# Revit family: Rohrschelle Titan HD, M16, Gummi
name_source: partatom
category: HLS-Bauteile
revit_build: Autodesk Revit 2017 (Build: 20190507_1515(x64)
units: mm (PartAtom-declared; Revit-internal decimal feet)

## family parameters
Arbeitsebenenbasiert = Ja
Beim Laden mit Abzugskörper schneiden = Nein
Bemaßung runder Anschluss = Durchmesser verwenden
Gemeinsam genutzt = Ja
Immer vertikal = Nein
Raumberechnungspunkt = Nein
Teiletyp = Normal

## types (33) — shared parameters
A = 26 mm  [stored 0.0853018 ft]
Anschluss = M16
Anschlußhöhe = 26 mm
Bauart = zweiteilig
Baustoffklasse = B2
Brandschutz = RAL GZ 656
DF1 = 29 mm  [stored 0.0951444 ft]
DS = 6 mm  [stored 0.019685 ft]
DVS = 13 mm
Dämmstärke = 6 mm  [stored 0.019685 ft]
Fabrikat = MEFA
Farbe Schalldämmeinlage = schwarz
Firma = MEFA Befestigungs- und Montagesysteme GmbH
HGA = 15 mm  [stored 0.0492126 ft]
Kurztext1 = Rohrschelle Titan HD 50x5,0
MB = 50 mm  [stored 0.164042 ft]
MD = 5 mm  [stored 0.0164042 ft]
Material = Stahl
Material Schalldämmeinlage = TPE
Materialmaße = 50x5,0 mm
Materialname = S235
Mengeneinheit = St
Oberflaeche = galvanisch verzinkt
Schalldämmeinlage = Gummi
Verschluss = Schraubverschluss
Verschluss-Schraube = M12
Vorgabe-Ansicht = 1219 mm
max. Temperaturbeständigkeit = 100 °C
max. zul. Last horizontal = 0.00 kN
max. zul. Last vertikal = 0.00 kN
vpe = 1 St
zero-valued in all types: Nennweite DN Rohr, Stärke Material, max. Rohraußendurchmesser, min. Rohraußendurchmesser

## per-type parameters (varying)
| type | Achsabstand | Artikelnummer | B | Breite | D | D0 | DF2 | EAN | Gewicht | Gewicht pro Bauteil | H | Höhe | Kurztext2 | R | RM | Rohraußendurchmesser | Rohraußendurchmesser Zoll | S | max. Höhe | max. zul. Last |
| Titan HD, M16, Ø 64, Gummi | 125 mm | 0071516 | 154 mm | 154 mm | 64 mm  [stored 0.209974 ft] | 76 mm  [stored 0.249344 ft] | 19 mm  [stored 0.062336 ft] | 4250928403261 | 0.94 kg | 0.94 kg | 101 mm | 101 mm | 64 mm M16 TPE | 38 mm  [stored 0.124672 ft] | 43 mm | 64 mm  [stored 0.209974 ft] | Zoll | 125 mm | 101 mm | 3.20 kN |
| Titan HD, M16, Ø 76, Gummi | 137 mm | 0071520 | 166 mm | 166 mm | 76 mm  [stored 0.249344 ft] | 88 mm  [stored 0.288714 ft] | 19 mm  [stored 0.062336 ft] | 4250928403285 | 1.03 kg | 1.03 kg | 113 mm | 113 mm | 76 mm M16 TPE | 44 mm  [stored 0.144357 ft] | 49 mm | 76 mm  [stored 0.249344 ft] | 2 1/2 Zoll | 137 mm | 113 mm | 3.20 kN |
| Titan HD, M16, Ø 89, Gummi | 150 mm | 0071522 | 179 mm | 179 mm | 89 mm  [stored 0.291995 ft] | 101 mm | 19 mm  [stored 0.062336 ft] | 4250928403308 | 1.12 kg | 1.12 kg | 126 mm | 126 mm | 89 mm M16 TPE | 51 mm | 56 mm | 89 mm  [stored 0.291995 ft] | 3 Zoll | 150 mm | 126 mm | 3.20 kN |
| Titan HD, M16, Ø108, Gummi | 169 mm | 0071528 | 199 mm | 198 mm | 108 mm | 120 mm | 20 mm  [stored 0.0656168 ft] | 4250928403322 | 1.27 kg | 1.27 kg | 145 mm | 145 mm | 108 mm M16 TPE | 60 mm  [stored 0.19685 ft] | 65 mm | 108 mm | Zoll | 170 mm | 145 mm | 3.20 kN |
| Titan HD, M16, Ø110, Gummi | 171 mm | 0071536 | 201 mm | 200 mm | 110 mm | 122 mm | 20 mm  [stored 0.0656168 ft] | 4250928403353 | 1.28 kg | 1.28 kg | 147 mm | 147 mm | 110 mm M16 TPE | 61 mm  [stored 0.200131 ft] | 66 mm | 110 mm | Zoll | 172 mm | 147 mm | 3.20 kN |
| Titan HD, M16, Ø133, Gummi | 195 mm | 0071609 | 224 mm | 224 mm | 133 mm | 145 mm | 20 mm  [stored 0.0656168 ft] | 4250928403414 | 1.45 kg | 1.45 kg | 170 mm | 170 mm | 133 mm M16 TPE | 73 mm | 78 mm | 133 mm | Zoll | 195 mm | 170 mm | 3.20 kN |
| Titan HD, M16, Ø135, Gummi | 197 mm | 0071617 | 226 mm | 226 mm | 135 mm | 147 mm | 20 mm  [stored 0.0656168 ft] | 4250928403438 | 1.47 kg | 1.47 kg | 172 mm | 172 mm | 135 mm M16 TPE | 74 mm | 79 mm | 135 mm | Zoll | 197 mm | 172 mm | 3.20 kN |
| Titan HD, M16, Ø140, Gummi | 202 mm | 0071625 | 231 mm | 231 mm | 140 mm | 152 mm | 20 mm  [stored 0.0656168 ft] | 4250928403445 | 1.51 kg | 1.51 kg | 177 mm | 177 mm | 140 mm M16 TPE | 76 mm  [stored 0.249344 ft] | 81 mm  [stored 0.265748 ft] | 140 mm | 5 Zoll | 202 mm | 177 mm | 3.20 kN |
| Titan HD, M16, Ø160, Gummi | 221 mm | 0071684 | 251 mm | 250 mm | 160 mm | 172 mm | 20 mm  [stored 0.0656168 ft] | 4250928403476 | 1.66 kg | 1.66 kg | 197 mm | 197 mm | 160 mm M16 TPE | 86 mm  [stored 0.282152 ft] | 91 mm  [stored 0.298556 ft] | 160 mm | Zoll | 222 mm | 197 mm | 3.20 kN |
| Titan HD, M16, Ø165, Gummi | 227 mm | 0071692 | 256 mm | 256 mm | 165 mm | 177 mm | 20 mm  [stored 0.0656168 ft] | 4250928403506 | 1.69 kg | 1.69 kg | 202 mm | 202 mm | 165 mm M16 TPE | 89 mm  [stored 0.291995 ft] | 94 mm | 165 mm | 6 Zoll | 227 mm | 202 mm | 3.20 kN |
| Titan HD, M16, Ø168, Gummi | 230 mm | 0071714 | 259 mm | 259 mm | 168 mm | 180 mm | 20 mm  [stored 0.0656168 ft] | 4250928403513 | 1.72 kg | 1.72 kg | 205 mm | 205 mm | 168 mm M16 TPE | 90 mm | 95 mm | 168 mm | Zoll | 230 mm | 205 mm | 3.20 kN |
| Titan HD, M16, Ø194, Gummi | 257 mm | 0071773 | 286 mm | 286 mm | 194 mm | 206 mm | 20 mm  [stored 0.0656168 ft] | 4250928403551 | 1.91 kg | 1.91 kg | 231 mm | 231 mm | 194 mm M16 TPE | 103 mm | 108 mm | 194 mm | Zoll | 257 mm | 231 mm | 11.50 kN |
| Titan HD, M16, Ø200, Gummi | 261 mm | 0071781 | 292 mm | 290 mm | 200 mm | 212 mm | 20 mm  [stored 0.0656168 ft] | 4250928403575 | 1.96 kg | 1.96 kg | 237 mm | 237 mm | 200 mm M16 TPE | 106 mm | 111 mm | 200 mm | Zoll | 263 mm | 237 mm | 11.50 kN |
| Titan HD, M16, Ø210, Gummi | 261 mm | 0071803 | 302 mm | 290 mm | 210 mm | 222 mm | 20 mm  [stored 0.0656168 ft] | 4250928403575 | 1.96 kg | 1.96 kg | 247 mm | 237 mm | 200 mm M16 TPE | 111 mm | 116 mm | 200 mm | Zoll | 273 mm | 237 mm | 11.50 kN |
| Titan HD, M16, Ø219, Gummi | 282 mm | 0071838 | 311 mm | 311 mm | 219 mm | 231 mm | 20 mm  [stored 0.0656168 ft] | 4250928403612 | 2.10 kg | 2.10 kg | 256 mm | 256 mm | 219 mm M16 TPE | 116 mm | 121 mm | 219 mm | 8 Zoll | 282 mm | 256 mm | 11.50 kN |
| Titan HD, M16, Ø267, Gummi | 330 mm | 0071897 | 359 mm | 359 mm | 267 mm | 279 mm | 20 mm  [stored 0.0656168 ft] | 4250928403650 | 2.46 kg | 2.46 kg | 304 mm | 304 mm | 267 mm M16 TPE | 140 mm | 145 mm | 267 mm | Zoll | 330 mm | 304 mm | 11.50 kN |
| Titan HD, M16, Ø273, Gummi | 336 mm | 0071900 | 365 mm | 365 mm | 273 mm | 285 mm | 20 mm  [stored 0.0656168 ft] | 4250928403674 | 2.50 kg | 2.50 kg | 310 mm | 310 mm | 273 mm M16 TPE | 143 mm | 148 mm | 273 mm | 10 Zoll | 336 mm | 310 mm | 11.50 kN |
| Titan HD, M16, Ø324, Gummi | 387 mm | 0071943 | 416 mm | 416 mm | 324 mm | 336 mm | 20 mm  [stored 0.0656168 ft] | 4250928403711 | 2.88 kg | 2.88 kg | 361 mm | 361 mm | 324 mm M16 TPE | 168 mm | 173 mm | 324 mm | 12 Zoll | 387 mm | 361 mm | 11.50 kN |
| Titan HD, M16, Ø356, Gummi | 419 mm | 0071978 | 448 mm | 448 mm | 356 mm | 368 mm | 20 mm  [stored 0.0656168 ft] | 4250928403735 | 3.12 kg | 3.12 kg | 393 mm | 393 mm | 356 mm M16 TPE | 184 mm | 189 mm | 356 mm | Zoll | 419 mm | 393 mm | 11.50 kN |
| Titan HD, M16, Ø368, Gummi | 431 mm | 0071986 | 460 mm | 460 mm | 368 mm | 380 mm | 20 mm  [stored 0.0656168 ft] | 4250928403759 | 3.21 kg | 3.21 kg | 405 mm | 405 mm | 368 mm M16 TPE | 190 mm | 195 mm | 368 mm | Zoll | 431 mm | 405 mm | 11.50 kN |
| Titan HD, M16, Ø114, Gummi | 175 mm | 0071552 | 205 mm | 204 mm | 114 mm | 126 mm | 20 mm  [stored 0.0656168 ft] | 4250928403360 | 1.31 kg | 1.31 kg | 151 mm | 151 mm | 114 mm M16 TPE | 63 mm  [stored 0.206693 ft] | 68 mm  [stored 0.223097 ft] | 114 mm | 4 Zoll | 176 mm | 151 mm | 3.20 kN |
| Titan HD, M16, Ø125, Gummi | 175 mm | 0071552 | 216 mm | 204 mm | 125 mm | 137 mm | 20 mm  [stored 0.0656168 ft] | 4250928403360 | 1.31 kg | 1.31 kg | 162 mm | 151 mm | 114 mm M16 TPE | 69 mm | 74 mm | 114 mm | 4 Zoll | 187 mm | 151 mm | 3.20 kN |
| Titan HD, M16, Ø127, Gummi | 188 mm | 0071595 | 218 mm | 217 mm | 127 mm | 139 mm | 20 mm  [stored 0.0656168 ft] | 4250928403391 | 1.41 kg | 1.41 kg | 164 mm | 164 mm | 127 mm M16 TPE | 70 mm | 75 mm | 127 mm | Zoll | 189 mm | 164 mm | 3.20 kN |
| Titan HD, M16, Ø152, Gummi | 214 mm | 0071641 | 243 mm | 243 mm | 152 mm | 164 mm | 20 mm  [stored 0.0656168 ft] | 4250928403452 | 1.60 kg | 1.60 kg | 189 mm | 189 mm | 152 mm M16 TPE | 82 mm  [stored 0.269029 ft] | 87 mm  [stored 0.285433 ft] | 152 mm | Zoll | 214 mm | 189 mm | 3.20 kN |
| Titan HD, M16, Ø177, Gummi | 239 mm | 0071730 | 268 mm | 268 mm | 177 mm | 189 mm | 20 mm  [stored 0.0656168 ft] | 4250928403520 | 1.78 kg | 1.78 kg | 214 mm | 214 mm | 177 mm M16 TPE | 95 mm | 100 mm | 177 mm | Zoll | 239 mm | 214 mm | 11.50 kN |
| Titan HD, M16, Ø180, Gummi | 242 mm | 0071757 | 271 mm | 271 mm | 180 mm | 192 mm | 20 mm  [stored 0.0656168 ft] | 4250928403537 | 1.81 kg | 1.81 kg | 217 mm | 217 mm | 180 mm M16 TPE | 96 mm | 101 mm | 180 mm | Zoll | 242 mm | 217 mm | 11.50 kN |
| Titan HD, M16, Ø225, Gummi | 286 mm | 0071846 | 317 mm | 315 mm | 225 mm | 237 mm | 20 mm  [stored 0.0656168 ft] | 4250928403629 | 2.14 kg | 2.14 kg | 262 mm | 262 mm | 225 mm M16 TPE | 119 mm | 124 mm | 225 mm | Zoll | 288 mm | 262 mm | 11.50 kN |
| Titan HD, M16, Ø245, Gummi | 308 mm | 0071870 | 337 mm | 337 mm | 245 mm | 257 mm | 20 mm  [stored 0.0656168 ft] | 4250928403636 | 2.29 kg | 2.29 kg | 282 mm | 282 mm | 245 mm M16 TPE | 129 mm | 134 mm | 245 mm | Zoll | 308 mm | 282 mm | 11.50 kN |
| Titan HD, M16, Ø280, Gummi | 343 mm | 0071927 | 372 mm | 372 mm | 280 mm | 292 mm | 20 mm  [stored 0.0656168 ft] | 4250928403681 | 2.56 kg | 2.56 kg | 317 mm | 317 mm | 280 mm M16 TPE | 146 mm | 151 mm | 280 mm | Zoll | 343 mm | 317 mm | 11.50 kN |
| Titan HD, M16, Ø298, Gummi | 361 mm | 0071935 | 390 mm | 390 mm | 298 mm | 310 mm | 20 mm  [stored 0.0656168 ft] | 4250928403698 | 2.69 kg | 2.69 kg | 335 mm | 335 mm | 298 mm M16 TPE | 155 mm | 160 mm | 298 mm | Zoll | 361 mm | 335 mm | 11.50 kN |
| Titan HD, M16, Ø406, Gummi | 469 mm | 0071994 | 498 mm | 498 mm | 406 mm | 418 mm | 20 mm  [stored 0.0656168 ft] | 4250928403773 | 3.50 kg | 3.50 kg | 443 mm | 443 mm | 406 mm M16 TPE | 209 mm | 214 mm | 406 mm | Zoll | 469 mm | 443 mm | 11.50 kN |
| Titan HD, M16, Ø457, Gummi | 520 mm | 0072003 | 549 mm | 549 mm | 457 mm | 469 mm | 20 mm  [stored 0.0656168 ft] | 4250928403780 | 3.88 kg | 3.88 kg | 494 mm | 494 mm | 457 mm M16 TPE | 235 mm | 240 mm | 457 mm | Zoll | 520 mm | 494 mm | 11.50 kN |
| Titan HD, M16, Ø508, Gummi | 571 mm | 0072014 | 600 mm | 600 mm | 508 mm | 520 mm | 20 mm  [stored 0.0656168 ft] | 4250928403803 | 4.26 kg | 4.26 kg | 545 mm | 545 mm | 508 mm M16 TPE | 260 mm | 265 mm | 508 mm | Zoll | 571 mm | 545 mm | 11.50 kN |

note: [stored X ft] marks values corroborated as IEEE doubles in the binary element streams (Revit-internal decimal feet)

## geometry (parser evidence)
native form markers: Sweep x5
no freeform markers — native parametric forms only
